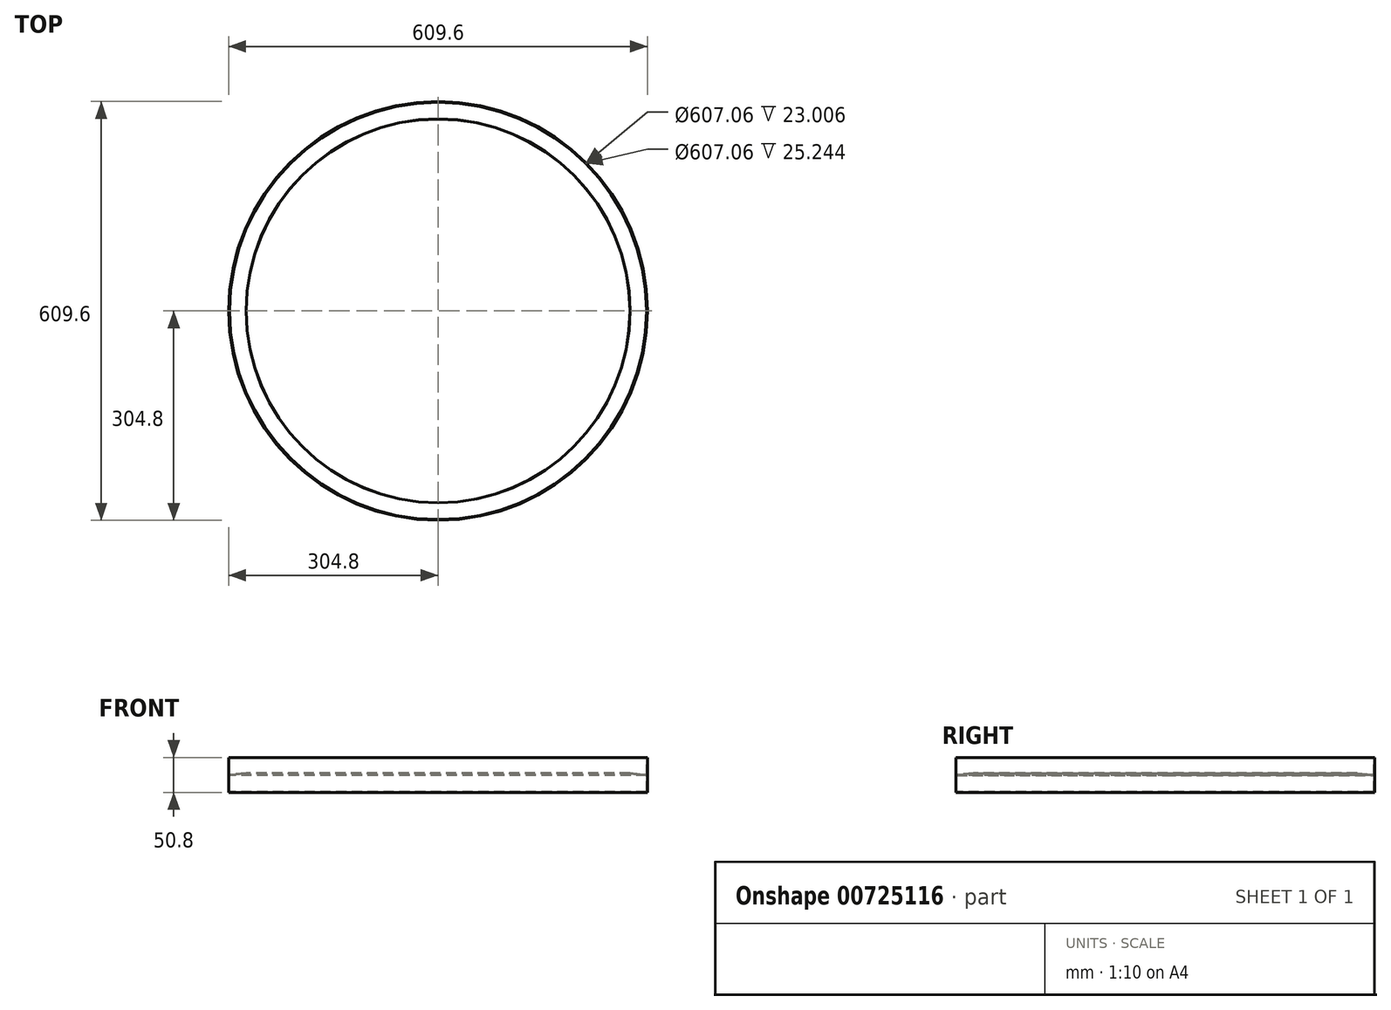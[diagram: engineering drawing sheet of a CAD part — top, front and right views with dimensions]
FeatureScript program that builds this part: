
annotation { "Feature Type Name" : "Feature", "Feature Type Description" : "" }
export const myFeature = defineFeature(function(context is Context, id is Id, definition is map)
    precondition{}
    {
        {
            var Q0;
            Q0=qCreatedBy(makeId("Front.planeOp"),FACE);
            var sketch = newSketch(context, id + "F0", { "sketchPlane" : qUnion([Q0])});
            skLineSegment(sketch, "E0.left", {"start": v(-304.8, -3.12) * mm, "end": v(-304.8, -28.52) * mm});
            skLineSegment(sketch, "E1", {"start": v(-279.4, 0) * mm, "end": v(-303.53, -2.96) * mm});
            skLineSegment(sketch, "E2", {"start": v(-279.4, 0) * mm, "end": v(-279.25, -1.26) * mm});
            skLineSegment(sketch, "E3", {"start": v(-279.25, -1.26) * mm, "end": v(-303.53, -4.24) * mm});
            skPoint(sketch, "E4.orphan", {"position": v(-304.8, 0) * mm});
            skLineSegment(sketch, "E5", {"start": v(-304.8, -3.12) * mm, "end": v(-304.8, 22.28) * mm});
            skLineSegment(sketch, "E6", {"start": v(-304.8, 22.28) * mm, "end": v(-303.53, 22.28) * mm});
            skLineSegment(sketch, "E7", {"start": v(-303.53, 22.28) * mm, "end": v(-303.53, -2.96) * mm});
            skLineSegment(sketch, "E8", {"start": v(-304.8, -28.52) * mm, "end": v(0, -28.52) * mm});
            skLineSegment(sketch, "E9", {"start": v(-303.53, -27.25) * mm, "end": v(-303.53, -4.24) * mm});
            skLineSegment(sketch, "E10", {"start": v(-303.53, -27.25) * mm, "end": v(0, -27.25) * mm});
            skLineSegment(sketch, "E11", {"start": v(0, -28.52) * mm, "end": v(0, -27.25) * mm});
            skSolve(sketch);
        }
        {
            var Q0;
            Q0=qCreatedBy(makeId("Front.planeOp"),FACE);
            var sketch = newSketch(context, id + "F1", { "sketchPlane" : qUnion([Q0])});
            skLineSegment(sketch, "E12", {"start": v(0, 40.5) * mm, "end": v(0, -62.38) * mm});
            skSolve(sketch);
        }
        {
            var Q0;
            Q0=makeQuery(id+"F0.imprint","IMPRINT",FACE,{"disambiguationData":[TD([[makeQuery(id+"F0.imprint","IMPRINT",EDGE,{"derivedFrom":sQuery(id+"F0.wireOp",EDGE,"E0.left")}),1.0]])]});
            var Q1;
            Q1=sQuery(id+"F1.wireOp",EDGE,"E12");
            revolve(context, id + "F2", {"surfaceOperationType" : NewSurfaceOperationType.NEW, "entities" : qUnion([Q0]), "axis" : qUnion([Q1]), "revolveType" : RevolveType.FULL});
        }
    });
